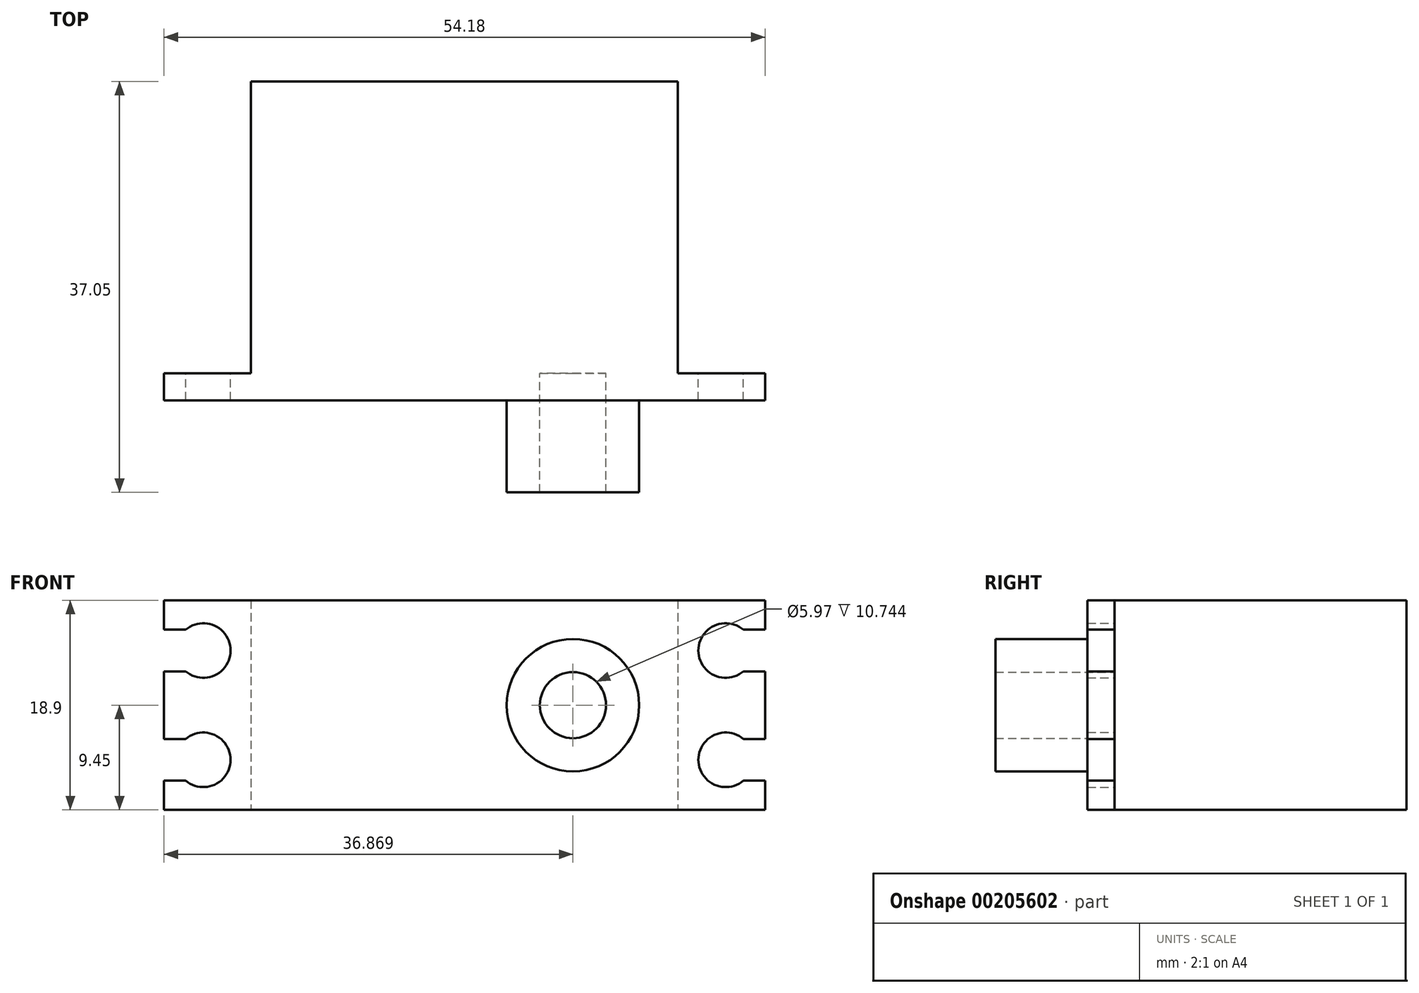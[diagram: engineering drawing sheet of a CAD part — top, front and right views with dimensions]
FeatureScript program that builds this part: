
annotation { "Feature Type Name" : "Feature", "Feature Type Description" : "" }
export const myFeature = defineFeature(function(context is Context, id is Id, definition is map)
    precondition{}
    {
        {
            var Q0;
            Q0=qCreatedBy(makeId("Front.planeOp"),FACE);
            var sketch = newSketch(context, id + "F0", { "sketchPlane" : qUnion([Q0])});
            skLineSegment(sketch, "E0.bottom", {"start": v(19.24, 9.45) * mm, "end": v(-19.24, 9.45) * mm});
            skLineSegment(sketch, "E0.top", {"start": v(19.24, -9.45) * mm, "end": v(-19.24, -9.45) * mm});
            skLineSegment(sketch, "E0.left", {"start": v(19.24, 9.45) * mm, "end": v(19.24, -9.45) * mm});
            skLineSegment(sketch, "E0.right", {"start": v(-19.24, 9.45) * mm, "end": v(-19.24, -9.45) * mm});
            skPoint(sketch, "E0.middle", {"position": v(0, 0) * mm});
            skSolve(sketch);
        }
        {
            var Q0;
            Q0=qSketchRegion(id+"F0",true);
            extrude(context, id + "F1", {"entities" : qUnion([Q0]), "oppositeDirection" : true, "depth" : 26.3 * mm});
        }
        {
            var Q0;
            Q0=qCreatedBy(makeId("Front.planeOp"),FACE);
            var sketch = newSketch(context, id + "F2", { "sketchPlane" : qUnion([Q0])});
            skLineSegment(sketch, "E1.bottom", {"start": v(27.09, 9.45) * mm, "end": v(-27.09, 9.45) * mm});
            skLineSegment(sketch, "E1.top", {"start": v(27.09, -9.45) * mm, "end": v(-27.09, -9.45) * mm});
            skLineSegment(sketch, "E1.left", {"start": v(27.09, 9.45) * mm, "end": v(27.09, 6.8) * mm});
            skLineSegment(sketch, "E1.right", {"start": v(-27.09, 9.45) * mm, "end": v(-27.09, 6.8) * mm});
            skPoint(sketch, "E1.middle", {"position": v(0, 0) * mm});
            skArc(sketch, "E2", {"start": v(-25.14, 3.05) * mm, "mid": v(-21.08, 4.93) * mm, "end": v(-25.14, 6.8) * mm});
            skArc(sketch, "E3", {"start": v(-25.14, -6.8) * mm, "mid": v(-21.08, -4.93) * mm, "end": v(-25.14, -3.05) * mm});
            skLineSegment(sketch, "E4.0", {"start": v(-25.14, 6.8) * mm, "end": v(-27.09, 6.8) * mm});
            skLineSegment(sketch, "E5.0", {"start": v(-25.14, 3.05) * mm, "end": v(-27.09, 3.05) * mm});
            skPoint(sketch, "E6.MirrorP", {"position": v(0, 13.61) * mm});
            skLineSegment(sketch, "E7.MirrorCS", {"start": v(-25.14, -6.8) * mm, "end": v(-27.09, -6.8) * mm});
            skLineSegment(sketch, "E8.MirrorCS", {"start": v(-25.14, -3.05) * mm, "end": v(-27.09, -3.05) * mm});
            skLineSegment(sketch, "E9.MirrorCS", {"start": v(25.14, 3.05) * mm, "end": v(27.09, 3.05) * mm});
            skLineSegment(sketch, "E10.MirrorCS", {"start": v(25.14, -3.05) * mm, "end": v(27.09, -3.05) * mm});
            skLineSegment(sketch, "E11.MirrorCS", {"start": v(25.14, -6.8) * mm, "end": v(27.09, -6.8) * mm});
            skLineSegment(sketch, "E12.MirrorCS", {"start": v(25.14, 6.8) * mm, "end": v(27.09, 6.8) * mm});
            skArc(sketch, "E13", {"start": v(25.14, 6.8) * mm, "mid": v(21.08, 4.93) * mm, "end": v(25.14, 3.05) * mm});
            skArc(sketch, "E14", {"start": v(25.14, -3.05) * mm, "mid": v(21.08, -4.93) * mm, "end": v(25.14, -6.8) * mm});
            skLineSegment(sketch, "E15", {"start": v(27.09, -6.8) * mm, "end": v(27.09, -9.45) * mm});
            skLineSegment(sketch, "E16", {"start": v(27.09, 3.05) * mm, "end": v(27.09, -3.05) * mm});
            skPoint(sketch, "E17.orphan", {"position": v(23.55, 3.05) * mm});
            skPoint(sketch, "E18.orphan", {"position": v(31.52, 3.05) * mm});
            skPoint(sketch, "E19.orphan", {"position": v(31.52, -3.05) * mm});
            skPoint(sketch, "E20.orphan", {"position": v(31.52, -6.8) * mm});
            skPoint(sketch, "E21.orphan", {"position": v(23.55, -3.05) * mm});
            skPoint(sketch, "E22.orphan", {"position": v(23.55, -6.8) * mm});
            skPoint(sketch, "E23.orphan", {"position": v(-31.52, 6.8) * mm});
            skPoint(sketch, "E24.orphan", {"position": v(-23.55, 6.8) * mm});
            skPoint(sketch, "E25.orphan", {"position": v(-23.55, 3.05) * mm});
            skPoint(sketch, "E26.orphan", {"position": v(-31.52, 3.05) * mm});
            skLineSegment(sketch, "E27.trimOffspring", {"start": v(-27.09, 3.05) * mm, "end": v(-27.09, -3.05) * mm});
            skLineSegment(sketch, "E28.trimOffspring", {"start": v(-27.09, -6.8) * mm, "end": v(-27.09, -9.45) * mm});
            skPoint(sketch, "E29.orphan", {"position": v(-23.55, -3.05) * mm});
            skPoint(sketch, "E30.orphan", {"position": v(-23.55, -6.8) * mm});
            skPoint(sketch, "E31.orphan", {"position": v(-31.52, -6.8) * mm});
            skPoint(sketch, "E32.orphan", {"position": v(-31.52, -3.05) * mm});
            skSolve(sketch);
        }
        {
            var Q0;
            Q0=qSketchRegion(id+"F2",true);
            extrude(context, id + "F3", {"entities" : qUnion([Q0]), "operationType" : NewBodyOperationType.ADD, "depth" : 2.44 * mm});
        }
        {
            var Q0;
            Q0=qCreatedBy(makeId("Front.planeOp"),FACE);
            var sketch = newSketch(context, id + "F4", { "sketchPlane" : qUnion([Q0])});
            skCircle(sketch, "E33", {"center": v(9.78, 0) * mm, "radius": 5.97 * mm});
            skSolve(sketch);
        }
        {
            var Q0;
            Q0=qSketchRegion(id+"F4",true);
            extrude(context, id + "F5", {"entities" : qUnion([Q0]), "operationType" : NewBodyOperationType.ADD, "depth" : 10.74 * mm});
        }
        {
            var Q0;
            Q0=qCreatedBy(makeId("Front.planeOp"),FACE);
            var sketch = newSketch(context, id + "F6", { "sketchPlane" : qUnion([Q0])});
            skCircle(sketch, "E34", {"center": v(9.78, 0) * mm, "radius": 2.98 * mm});
            skSolve(sketch);
        }
        {
            var Q0;
            Q0=qSketchRegion(id+"F6",true);
            extrude(context, id + "F7", {"entities" : qUnion([Q0]), "operationType" : NewBodyOperationType.REMOVE, "depth" : 14.2 * mm});
        }
    });
